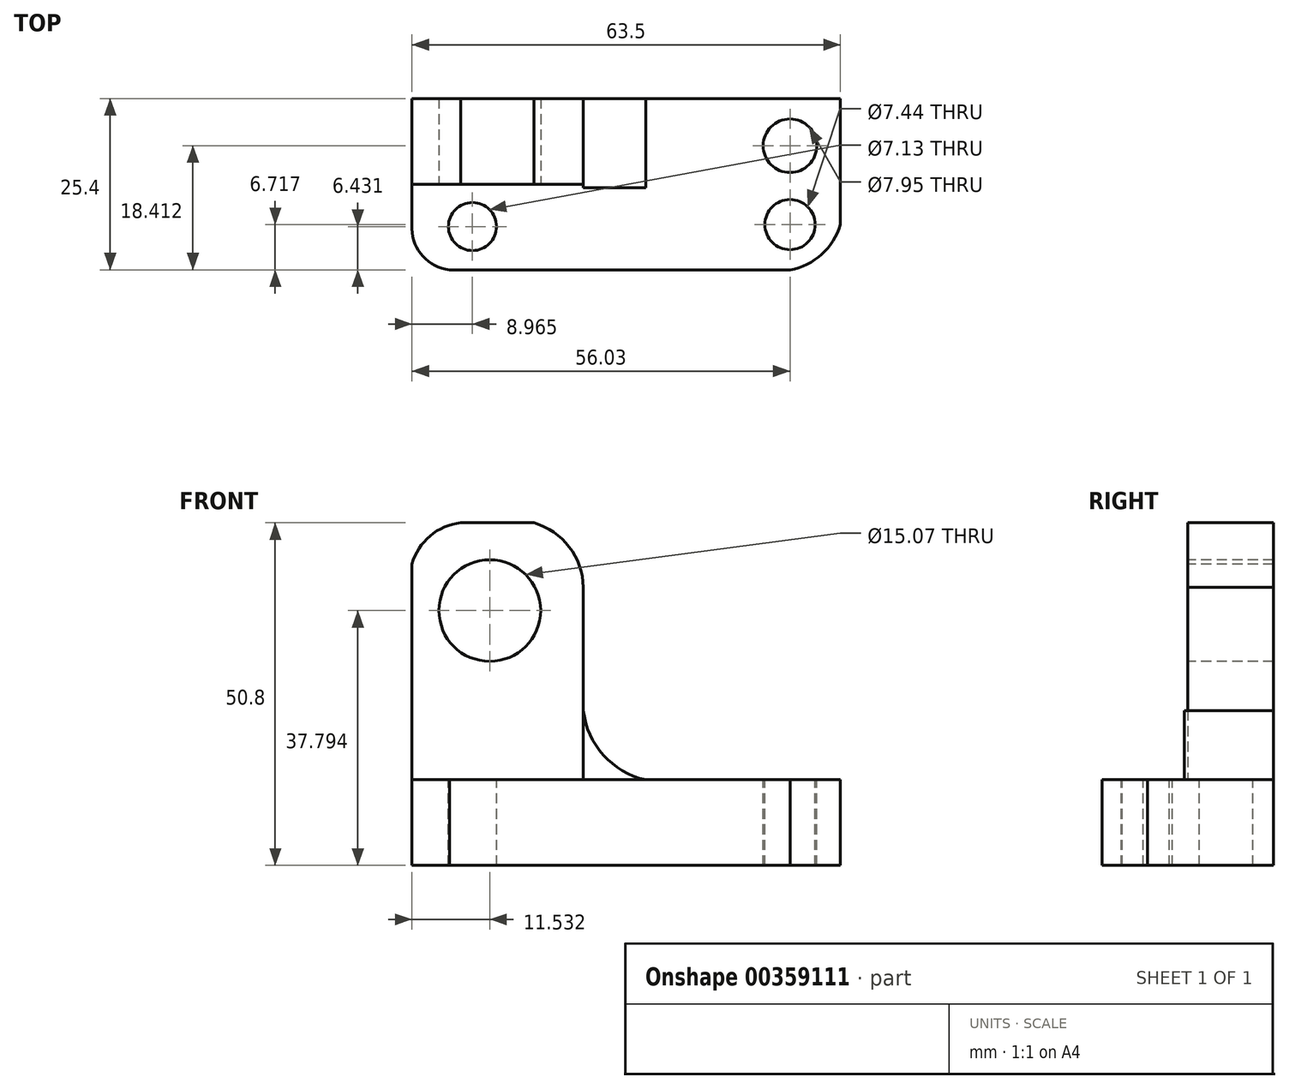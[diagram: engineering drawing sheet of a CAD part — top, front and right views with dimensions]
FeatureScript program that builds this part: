
annotation { "Feature Type Name" : "Feature", "Feature Type Description" : "" }
export const myFeature = defineFeature(function(context is Context, id is Id, definition is map)
    precondition{}
    {
        {
            var Q0;
            Q0=qCreatedBy(makeId("Front.planeOp"),FACE);
            var sketch = newSketch(context, id + "F0", { "sketchPlane" : qUnion([Q0])});
            skLineSegment(sketch, "E0", {"start": v(-56.03, 0) * mm, "end": v(-56.03, 50.8) * mm});
            skLineSegment(sketch, "E1", {"start": v(-56.03, 50.8) * mm, "end": v(-30.63, 50.8) * mm});
            skLineSegment(sketch, "E2", {"start": v(-30.63, 50.8) * mm, "end": v(-30.63, 12.7) * mm});
            skLineSegment(sketch, "E3", {"start": v(-30.63, 12.7) * mm, "end": v(7.47, 12.7) * mm});
            skLineSegment(sketch, "E4", {"start": v(7.47, 12.7) * mm, "end": v(7.47, 0) * mm});
            skLineSegment(sketch, "E5", {"start": v(7.47, 0) * mm, "end": v(-56.03, 0) * mm});
            skSolve(sketch);
        }
        {
            var Q0;
            Q0 = qSketchRegion(id + "F0", true);
            extrude(context, id + "F1", {"entities" : qUnion([Q0]), "depth" : 25.4 * mm});
        }
        {
            var Q0;
            Q0=makeQuery(id+"F1.opExtrude","CAP_FACE",FACE,{"disambiguationData":[OSD([sQuery(id+"F0.wireOp",EDGE,"E0"),sQuery(id+"F0.wireOp",EDGE,"E1"),sQuery(id+"F0.wireOp",EDGE,"E2"),sQuery(id+"F0.wireOp",EDGE,"E3"),sQuery(id+"F0.wireOp",EDGE,"E4"),sQuery(id+"F0.wireOp",EDGE,"E5")])],"isStart":false});
            var sketch = newSketch(context, id + "F2", { "sketchPlane" : qUnion([Q0])});
            skArc(sketch, "E6", {"start": v(-48.78, 50.8) * mm, "mid": v(-54.9, 47.13) * mm, "end": v(-56.03, 40.08) * mm});
            skArc(sketch, "E7", {"start": v(-30.63, 41.22) * mm, "mid": v(-32.71, 47.2) * mm, "end": v(-37.94, 50.8) * mm});
            skSolve(sketch);
        }
        {
            var Q0;
            {var subQ0=sQuery(id+"F2.wireOp",EDGE,"E6");var subQ1=makeQuery(id+"F1.opExtrude","CAP_EDGE",EDGE,{"disambiguationData":[OSD([sQuery(id+"F0.wireOp",EDGE,"E1")])],"isStart":false});var subQ2=makeQuery(id+"F2.imprint","INTERSECT",VERTEX,{"derivedFrom":[subQ1,subQ0]});Q0=makeQuery(id+"F2.imprint","IMPRINT",FACE,{"disambiguationData":[TD([[makeQuery(id+"F2.imprint","IMPRINT",EDGE,{"disambiguationData":[TD([[subQ2,-1.0]])],"derivedFrom":subQ0}),-1.0]])]});}
            var Q1;
            {var subQ0=sQuery(id+"F2.wireOp",EDGE,"E7");Q1=makeQuery(id+"F2.imprint","IMPRINT",FACE,{"disambiguationData":[TD([[makeQuery(id+"F2.imprint","IMPRINT",EDGE,{"derivedFrom":subQ0}),-1.0]])]});}
            extrude(context, id + "F3", {"entities" : qUnion([Q0, Q1]), "operationType" : NewBodyOperationType.REMOVE, "oppositeDirection" : true, "depth" : 25.4 * mm});
        }
        {
            var Q0;
            Q0=makeQuery(id+"F1.opExtrude","CAP_FACE",FACE,{"disambiguationData":[OSD([sQuery(id+"F0.wireOp",EDGE,"E0"),sQuery(id+"F0.wireOp",EDGE,"E1"),sQuery(id+"F0.wireOp",EDGE,"E2"),sQuery(id+"F0.wireOp",EDGE,"E3"),sQuery(id+"F0.wireOp",EDGE,"E4"),sQuery(id+"F0.wireOp",EDGE,"E5")])],"isStart":false});
            var sketch = newSketch(context, id + "F4", { "sketchPlane" : qUnion([Q0])});
            skLineSegment(sketch, "E8", {"start": v(-30.63, 12.7) * mm, "end": v(-56.03, 12.7) * mm});
            skSolve(sketch);
        }
        {
            var Q0;
            {var subQ1=sQuery(id+"F4.wireOp",EDGE,"E8");Q0=makeQuery(id+"F4.imprint","IMPRINT",FACE,{"disambiguationData":[TD([[makeQuery(id+"F4.imprint","IMPRINT",EDGE,{"derivedFrom":subQ1}),-1.0]])]});}
            var Q1;
            Q1 = qSketchRegion(id + "F6", true);
            extrude(context, id + "F5", {"entities" : qUnion([Q0, Q1]), "operationType" : NewBodyOperationType.REMOVE, "oppositeDirection" : true, "depth" : 12.7 * mm});
        }
        {
            var Q0;
            Q0=makeQuery(id+"F5.boolean.opBoolean","COPY",FACE,{"derivedFrom":makeQuery(id+"F5.opExtrude","CAP_FACE",FACE,{"disambiguationData":[OSD([sQuery(id+"F0.wireOp",EDGE,"E0"),sQuery(id+"F0.wireOp",EDGE,"E1"),sQuery(id+"F0.wireOp",EDGE,"E2"),sQuery(id+"F2.wireOp",EDGE,"E6"),sQuery(id+"F2.wireOp",EDGE,"E7"),sQuery(id+"F4.wireOp",EDGE,"E8")])],"isStart":false})});
            var sketch = newSketch(context, id + "F6", { "sketchPlane" : qUnion([Q0])});
            skCircle(sketch, "E9", {"center": v(-44.5, 37.8) * mm, "radius": 7.54 * mm});
            skSolve(sketch);
        }
        {
            var Q0;
            Q0=makeQuery(id+"F6.imprint","IMPRINT",FACE,{"disambiguationData":[TD([[makeQuery(id+"F6.imprint","IMPRINT",EDGE,{"derivedFrom":sQuery(id+"F6.wireOp",EDGE,"E9")}),1.0]])]});
            extrude(context, id + "F7", {"entities" : qUnion([Q0]), "operationType" : NewBodyOperationType.REMOVE, "oppositeDirection" : true, "depth" : 25.4 * mm});
        }
        {
            var Q0;
            Q0=makeQuery(id+"F5.boolean.opBoolean","MERGE",FACE,{"derivedFrom":[makeQuery(id+"F1.opExtrude","SWEPT_FACE",FACE,{"disambiguationData":[OSD([sQuery(id+"F0.wireOp",EDGE,"E3")])]}),makeQuery(id+"F5.opExtrude","SWEPT_FACE",FACE,{"disambiguationData":[OSD([sQuery(id+"F4.wireOp",EDGE,"E8")])]})]});
            var sketch = newSketch(context, id + "F8", { "sketchPlane" : qUnion([Q0])});
            skArc(sketch, "E10", {"start": v(0, -25.4) * mm, "mid": v(4.69, -23.1) * mm, "end": v(7.47, -18.68) * mm});
            skArc(sketch, "E11", {"start": v(-56.03, -19.05) * mm, "mid": v(-54.48, -23.3) * mm, "end": v(-50.49, -25.4) * mm});
            skSolve(sketch);
        }
        {
            var Q0;
            {var subQ0=sQuery(id+"F8.wireOp",EDGE,"E11");var subQ1=sQuery(id+"F4.wireOp",EDGE,"E8");var subQ2=makeQuery(id+"F5.boolean.opBoolean","MERGE",EDGE,{"derivedFrom":[makeQuery(id+"F1.opExtrude","CAP_EDGE",EDGE,{"disambiguationData":[OSD([sQuery(id+"F0.wireOp",EDGE,"E3")])],"isStart":false}),makeQuery(id+"F5.opExtrude","CAP_EDGE",EDGE,{"disambiguationData":[OSD([subQ1])],"isStart":true})]});var subQ3=makeQuery(id+"F8.imprint","INTERSECT",VERTEX,{"derivedFrom":[subQ2,subQ0]});Q0=makeQuery(id+"F8.imprint","IMPRINT",FACE,{"disambiguationData":[TD([[makeQuery(id+"F8.imprint","IMPRINT",EDGE,{"disambiguationData":[TD([[subQ3,1.0]])],"derivedFrom":subQ0}),-1.0]])]});}
            var Q1;
            {var subQ0=sQuery(id+"F8.wireOp",EDGE,"E10");Q1=makeQuery(id+"F8.imprint","IMPRINT",FACE,{"disambiguationData":[TD([[makeQuery(id+"F8.imprint","IMPRINT",EDGE,{"derivedFrom":subQ0}),-1.0]])]});}
            extrude(context, id + "F9", {"entities" : qUnion([Q0, Q1]), "operationType" : NewBodyOperationType.REMOVE, "oppositeDirection" : true, "depth" : 25.4 * mm});
        }
        {
            var Q0;
            Q0=makeQuery(id+"F1.opExtrude","CAP_FACE",FACE,{"disambiguationData":[OSD([sQuery(id+"F0.wireOp",EDGE,"E0"),sQuery(id+"F0.wireOp",EDGE,"E1"),sQuery(id+"F0.wireOp",EDGE,"E2"),sQuery(id+"F0.wireOp",EDGE,"E3"),sQuery(id+"F0.wireOp",EDGE,"E4"),sQuery(id+"F0.wireOp",EDGE,"E5")])],"isStart":true});
            var sketch = newSketch(context, id + "F10", { "sketchPlane" : qUnion([Q0])});
            skArc(sketch, "E12", {"start": v(21.4, 12.7) * mm, "mid": v(27.65, 16.36) * mm, "end": v(30.63, 22.96) * mm});
            skSolve(sketch);
        }
        {
            var Q0;
            {var subQ0=sQuery(id+"F10.wireOp",EDGE,"E12");Q0=makeQuery(id+"F10.imprint","IMPRINT",FACE,{"disambiguationData":[TD([[makeQuery(id+"F10.imprint","IMPRINT",EDGE,{"derivedFrom":subQ0}),-1.0]])]});}
            extrude(context, id + "F11", {"entities" : qUnion([Q0]), "operationType" : NewBodyOperationType.ADD, "oppositeDirection" : true, "depth" : 13.2 * mm});
        }
        {
            var Q0;
            Q0=makeQuery(id+"F5.boolean.opBoolean","MERGE",FACE,{"derivedFrom":[makeQuery(id+"F1.opExtrude","SWEPT_FACE",FACE,{"disambiguationData":[OSD([sQuery(id+"F0.wireOp",EDGE,"E3")])]}),makeQuery(id+"F5.opExtrude","SWEPT_FACE",FACE,{"disambiguationData":[OSD([sQuery(id+"F4.wireOp",EDGE,"E8")])]})]});
            var sketch = newSketch(context, id + "F12", { "sketchPlane" : qUnion([Q0])});
            skCircle(sketch, "E13", {"center": v(-47.06, -18.97) * mm, "radius": 3.57 * mm});
            skCircle(sketch, "E14", {"center": v(0, -18.68) * mm, "radius": 3.72 * mm});
            skSolve(sketch);
        }
        {
            var Q0;
            Q0=makeQuery(id+"F12.imprint","IMPRINT",FACE,{"disambiguationData":[TD([[makeQuery(id+"F12.imprint","IMPRINT",EDGE,{"derivedFrom":sQuery(id+"F12.wireOp",EDGE,"E13")}),1.0]])]});
            var Q1;
            Q1=makeQuery(id+"F12.imprint","IMPRINT",FACE,{"disambiguationData":[TD([[makeQuery(id+"F12.imprint","IMPRINT",EDGE,{"derivedFrom":sQuery(id+"F12.wireOp",EDGE,"E14")}),1.0]])]});
            extrude(context, id + "F13", {"entities" : qUnion([Q0, Q1]), "operationType" : NewBodyOperationType.REMOVE, "oppositeDirection" : true, "depth" : 25.4 * mm});
        }
        {
            var Q0;
            Q0=makeQuery(id+"F5.boolean.opBoolean","MERGE",FACE,{"derivedFrom":[makeQuery(id+"F1.opExtrude","SWEPT_FACE",FACE,{"disambiguationData":[OSD([sQuery(id+"F0.wireOp",EDGE,"E3")])]}),makeQuery(id+"F5.opExtrude","SWEPT_FACE",FACE,{"disambiguationData":[OSD([sQuery(id+"F4.wireOp",EDGE,"E8")])]})]});
            var sketch = newSketch(context, id + "F14", { "sketchPlane" : qUnion([Q0])});
            skCircle(sketch, "E15", {"center": v(0, -6.99) * mm, "radius": 3.97 * mm});
            skSolve(sketch);
        }
        {
            var Q0;
            Q0=makeQuery(id+"F14.imprint","IMPRINT",FACE,{"disambiguationData":[TD([[makeQuery(id+"F14.imprint","IMPRINT",EDGE,{"derivedFrom":sQuery(id+"F14.wireOp",EDGE,"E15")}),1.0]])]});
            extrude(context, id + "F15", {"entities" : qUnion([Q0]), "operationType" : NewBodyOperationType.REMOVE, "oppositeDirection" : true, "depth" : 25.4 * mm});
        }
    });
